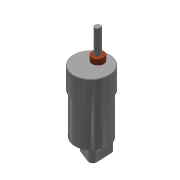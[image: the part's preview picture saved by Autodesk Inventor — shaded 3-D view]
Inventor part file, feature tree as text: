
AUTODESK INVENTOR PART (.ipt)
format: ipt  version: 2013 (Build 170138000, 138)  size: 240,640 bytes
history: native  units: in
note: dims shown in document units (in); Inventor stores cm internally (conversion verified against a paired STEP export)
features: extrude x4, sketch x4, fillet x2, other x1, imported_body x1
ambient origin geometry x8: Origin, YZ Plane, XZ Plane, XY Plane, X Axis, Y Axis, Z Axis, Center Point
bodies: Solid2 (feature_tree)
feature tree (12):
  other  "DC_MOTOR_2011"
  imported_body  "Base1"
  extrude  "Extrusion1"  Depth=0.5909in
  extrude  "Extrusion2"  Depth=0.4528in
  extrude  "Extrusion3"  Depth=0.1654in TaperAngle=0.0deg
  fillet  "Fillet1"  Radius=0.748in
  fillet  "Fillet2"  Radius=0.4331in
  extrude  "Extrusion4"  Depth=0.2165in
  sketch  "Sketch1"  dims[d0=0.315in d1=0.5909in]
  sketch  "Sketch2"  dims[d3=0.3436in d5=0.4528in]
  sketch  "Sketch3"  dims[d6=0.4528in d7=0.1654in d8=0.0in d9=0.748in d11=0.4331in]
  sketch  "Sketch4"  dims[d12=0.3661in d13=0.0in d14=0.2165in d16=0.0472in d17=0.0in d18=0.0197in d19=0.0787in d20=0.1181in d21=0.1181in d22=0.5906in d23=0.0in]
